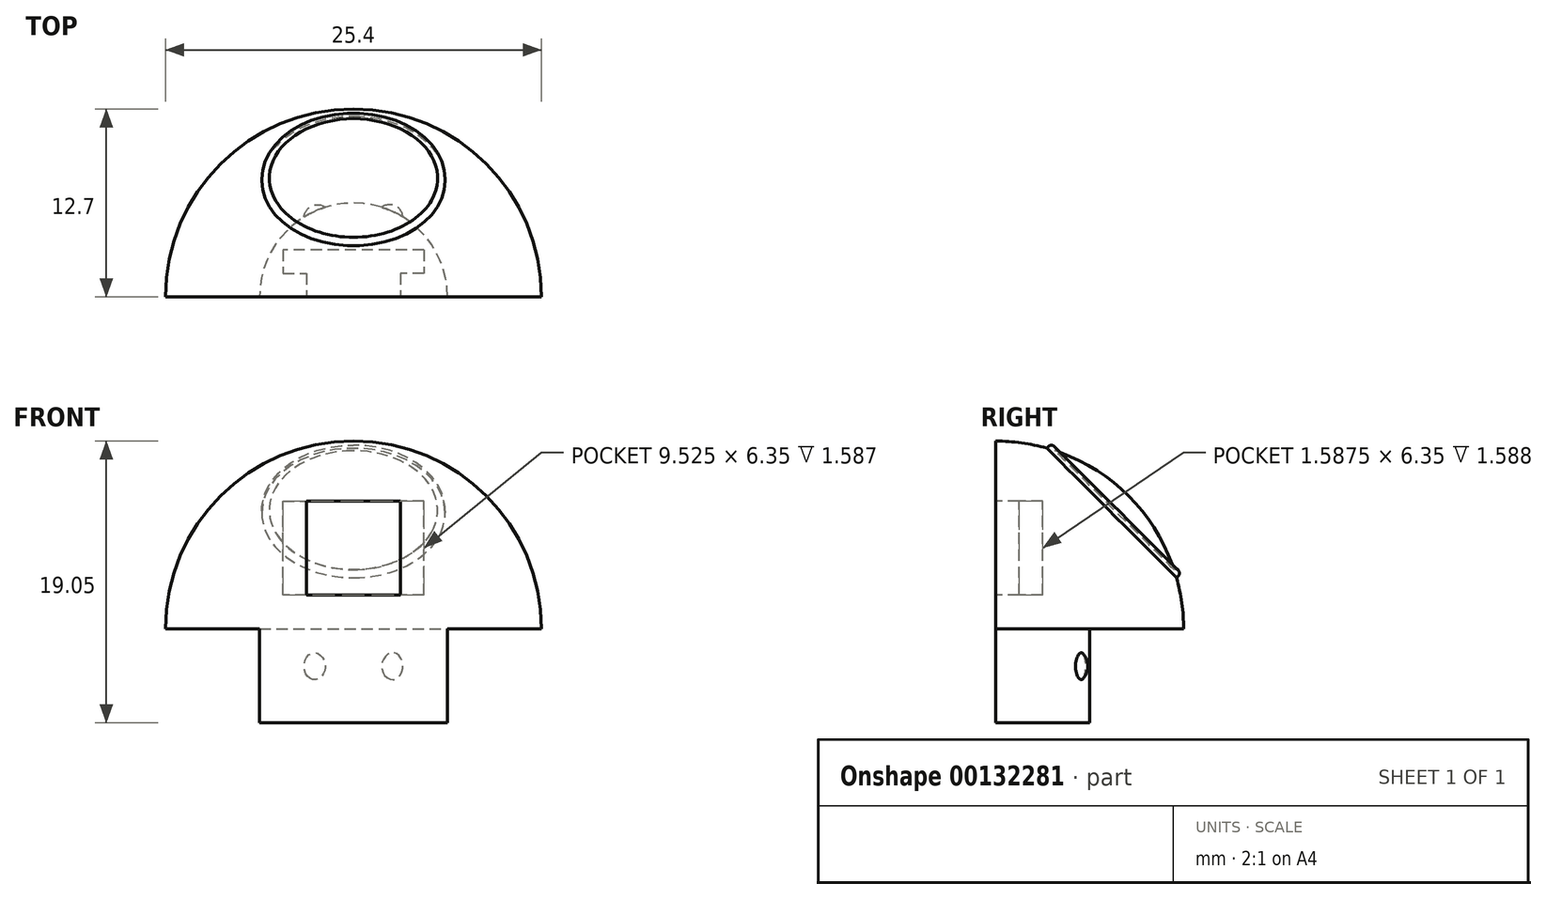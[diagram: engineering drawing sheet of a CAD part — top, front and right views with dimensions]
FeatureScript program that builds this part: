
annotation { "Feature Type Name" : "Feature", "Feature Type Description" : "" }
export const myFeature = defineFeature(function(context is Context, id is Id, definition is map)
    precondition{}
    {
        {
            var Q0;
            Q0=qCreatedBy(makeId("Front.planeOp"),FACE);
            var sketch = newSketch(context, id + "F0", { "sketchPlane" : qUnion([Q0])});
            skArc(sketch, "E0", {"start": v(12.7, 0) * mm, "mid": v(0, 12.7) * mm, "end": v(-12.7, 0) * mm});
            skLineSegment(sketch, "E1", {"start": v(-12.7, 0) * mm, "end": v(-6.35, 0) * mm});
            skLineSegment(sketch, "E2", {"start": v(6.35, 0) * mm, "end": v(12.7, 0) * mm});
            skLineSegment(sketch, "E3.0", {"start": v(-6.35, 0) * mm, "end": v(-6.35, -6.35) * mm});
            skLineSegment(sketch, "E4.0", {"start": v(6.35, 0) * mm, "end": v(6.35, -6.35) * mm});
            skLineSegment(sketch, "E5", {"start": v(6.35, -6.35) * mm, "end": v(-6.35, -6.35) * mm});
            skLineSegment(sketch, "E6", {"start": v(0, 0) * mm, "end": v(0, -6.35) * mm});
            skLineSegment(sketch, "E7", {"start": v(0, -6.35) * mm, "end": v(0, 12.7) * mm});
            skSolve(sketch);
        }
        {
            var Q0;
            {var subQ1=sQuery(id+"F0.wireOp",EDGE,"E4.0");Q0=makeQuery(id+"F0.imprint","IMPRINT",FACE,{"disambiguationData":[TD([[makeQuery(id+"F0.imprint","IMPRINT",EDGE,{"derivedFrom":subQ1}),-1.0]])]});}
            var Q1;
            Q1=sQuery(id+"F0.wireOp",EDGE,"E7");
            revolve(context, id + "F1", {"entities" : qUnion([Q0]), "axis" : qUnion([Q1]), "revolveType" : RevolveType.ONE_DIRECTION, "angle" : 180 * degree});
        }
        {
            var Q0;
            Q0=makeQuery(id+"F1.opRevolve","CAP_FACE",FACE,{"disambiguationData":[OSD([sQuery(id+"F0.wireOp",EDGE,"E0"),sQuery(id+"F0.wireOp",EDGE,"E4.0"),sQuery(id+"F0.wireOp",EDGE,"E2"),sQuery(id+"F0.wireOp",EDGE,"E5"),sQuery(id+"F0.wireOp",EDGE,"E7")])],"isStart":false});
            var sketch = newSketch(context, id + "F2", { "sketchPlane" : qUnion([Q0])});
            skSolve(sketch);
        }
        {
            var Q0;
            Q0=makeQuery(id+"F1.opRevolve","CAP_FACE",FACE,{"disambiguationData":[OSD([sQuery(id+"F0.wireOp",EDGE,"E0"),sQuery(id+"F0.wireOp",EDGE,"E4.0"),sQuery(id+"F0.wireOp",EDGE,"E2"),sQuery(id+"F0.wireOp",EDGE,"E5"),sQuery(id+"F0.wireOp",EDGE,"E7")])],"isStart":false});
            cPlane(context, id + "F3", {"entities" : qUnion([Q0]), "cplaneType" : CPlaneType.OFFSET, "offset" : 5.33 * mm, "oppositeDirection" : true, "width" : 152.4 * mm, "height" : 152.4 * mm});
        }
        {
            var Q0;
            Q0=qCreatedBy(id+"F3.planeOp",FACE);
            var sketch = newSketch(context, id + "F4", { "sketchPlane" : qUnion([Q0])});
            skArc(sketch, "E8.0", {"start": v(2.44, -3.7) * mm, "mid": v(1.54, -2.52) * mm, "end": v(2.44, -1.35) * mm});
            skLineSegment(sketch, "E8.1", {"start": v(2.44, -1.35) * mm, "end": v(2.44, -3.7) * mm});
            skPoint(sketch, "E8.2.end.orphan", {"position": v(2.44, -1.35) * mm});
            skPoint(sketch, "E8.2.start.orphan", {"position": v(2.44, -3.7) * mm});
            skSolve(sketch);
        }
        {
            var Q0;
            Q0 = qSketchRegion(id + "F4", true);
            var Q1;
            Q1=sQuery(id+"F4.wireOp",EDGE,"E8.1");
            revolve(context, id + "F5", {"operationType" : NewBodyOperationType.ADD, "entities" : qUnion([Q0]), "axis" : qUnion([Q1]), "revolveType" : RevolveType.FULL});
        }
        {
            var Q0;
            Q0=qCreatedBy(id+"F3.planeOp",FACE);
            var sketch = newSketch(context, id + "F6", { "sketchPlane" : qUnion([Q0])});
            skLineSegment(sketch, "E9.0", {"start": v(-2.44, -1.35) * mm, "end": v(-2.44, -3.7) * mm});
            skArc(sketch, "E9.1", {"start": v(-2.44, -3.7) * mm, "mid": v(-1.54, -2.52) * mm, "end": v(-2.44, -1.35) * mm});
            skSolve(sketch);
        }
        {
            var Q0;
            Q0 = qSketchRegion(id + "F6", true);
            var Q1;
            Q1=sQuery(id+"F6.wireOp",EDGE,"E9.0");
            revolve(context, id + "F7", {"operationType" : NewBodyOperationType.ADD, "entities" : qUnion([Q0]), "axis" : qUnion([Q1]), "revolveType" : RevolveType.FULL});
        }
        {
            var Q0;
            Q0=qCreatedBy(makeId("Right.planeOp"),FACE);
            var sketch = newSketch(context, id + "F8", { "sketchPlane" : qUnion([Q0])});
            skLineSegment(sketch, "E10.0", {"start": v(0, 0) * mm, "end": v(0, 12.7) * mm});
            skLineSegment(sketch, "E10.1", {"start": v(0, 0) * mm, "end": v(12.7, 0) * mm});
            skSolve(sketch);
        }
        {
            var Q0;
            Q0=makeQuery(id+"F2.imprint","IMPRINT",FACE,{"disambiguationData":[TD([[makeQuery(id+"F2.imprint","IMPRINT",EDGE,{"derivedFrom":makeQuery(id+"F1.opRevolve","CAP_EDGE",EDGE,{"disambiguationData":[OSD([sQuery(id+"F0.wireOp",EDGE,"E0")])],"isStart":false})}),-1.0]])]});
            cPlane(context, id + "F9", {"entities" : qUnion([Q0]), "cplaneType" : CPlaneType.OFFSET, "offset" : 6.35 * mm, "oppositeDirection" : true, "width" : 152.4 * mm, "height" : 152.4 * mm});
        }
        {
            var Q0;
            Q0=qCreatedBy(id+"F9.planeOp",FACE);
            var sketch = newSketch(context, id + "F10", { "sketchPlane" : qUnion([Q0])});
            skPoint(sketch, "E11.0", {"position": v(0, 0) * mm});
            skLineSegment(sketch, "E12.0", {"start": v(12.7, 0) * mm, "end": v(-12.7, 0) * mm});
            skLineSegment(sketch, "E12.1", {"start": v(0, 0) * mm, "end": v(0, 12.7) * mm});
            skLineSegment(sketch, "E13", {"start": v(0, 6.35) * mm, "end": v(13.47, 6.35) * mm});
            skPoint(sketch, "E13.endSnap0", {"position": v(0, 6.35) * mm});
            skSolve(sketch);
        }
        {
            var Q0;
            Q0=sQuery(id+"F8.wireOp",VERTEX,"E10.0.end");
            var Q1;
            Q1=sQuery(id+"F8.wireOp",VERTEX,"E10.1.end");
            var Q2;
            Q2=sQuery(id+"F10.wireOp",VERTEX,"E13.end");
            cPlane(context, id + "F11", {"entities" : qUnion([Q0, Q1, Q2]), "cplaneType" : CPlaneType.THREE_POINT, "offset" : 0 * mm, "width" : 152.4 * mm, "height" : 152.4 * mm});
        }
        {
            var Q0;
            Q0=qCreatedBy(id+"F11.planeOp",FACE);
            var sketch = newSketch(context, id + "F12", { "sketchPlane" : qUnion([Q0])});
            skCircle(sketch, "E14", {"center": v(0, 0) * mm, "radius": 5.69 * mm});
            skCircle(sketch, "E15.0", {"center": v(0, 0) * mm, "radius": 6.2 * mm});
            skSolve(sketch);
        }
        {
            var Q0;
            Q0 = qSketchRegion(id + "F12", true);
            extrude(context, id + "F13", {"entities" : qUnion([Q0]), "operationType" : NewBodyOperationType.ADD, "depth" : 2.54 * mm});
        }
        {
            var Q0;
            Q0=makeQuery(id+"F13.opExtrude","CAP_EDGE",EDGE,{"disambiguationData":[OSD([sQuery(id+"F12.wireOp",EDGE,"E15.0")])],"isStart":false});
            var Q1;
            Q1=makeQuery(id+"F13.opExtrude","CAP_EDGE",EDGE,{"disambiguationData":[OSD([sQuery(id+"F12.wireOp",EDGE,"E14")])],"isStart":false});
            fillet(context, id + "F14", {"entities" : qUnion([Q0, Q1]), "radius" : 0.25 * mm, "tangentPropagation" : true, "allowEdgeOverflow" : false});
        }
        {
            var Q0;
            Q0=qCreatedBy(makeId("Right.planeOp"),FACE);
            cPlane(context, id + "F15", {"entities" : qUnion([Q0]), "cplaneType" : CPlaneType.OFFSET, "offset" : 5.08 * mm, "width" : 152.4 * mm, "height" : 152.4 * mm});
        }
        {
            var Q0;
            Q0=qCreatedBy(id+"F15.planeOp",FACE);
            var sketch = newSketch(context, id + "F16", { "sketchPlane" : qUnion([Q0])});
            skArc(sketch, "E16", {"start": v(0, 1.12) * mm, "mid": v(5.2, 6.33) * mm, "end": v(0, 11.54) * mm});
            skArc(sketch, "E17", {"start": v(0, 0.68) * mm, "mid": v(5.66, 6.33) * mm, "end": v(0, 11.99) * mm});
            skLineSegment(sketch, "E18", {"start": v(0, 11.54) * mm, "end": v(0, 1.12) * mm});
            skLineSegment(sketch, "E19", {"start": v(0, 11.99) * mm, "end": v(0, 0.68) * mm});
            skSolve(sketch);
        }
        {
            var Q0;
            Q0=qCreatedBy(makeId("Right.planeOp"),FACE);
            cPlane(context, id + "F17", {"entities" : qUnion([Q0]), "cplaneType" : CPlaneType.OFFSET, "offset" : 5.08 * mm, "oppositeDirection" : true, "width" : 152.4 * mm, "height" : 152.4 * mm});
        }
        {
            var Q0;
            Q0=makeQuery(id+"F1.opRevolve","CAP_FACE",FACE,{"disambiguationData":[OSD([sQuery(id+"F0.wireOp",EDGE,"E0"),sQuery(id+"F0.wireOp",EDGE,"E4.0"),sQuery(id+"F0.wireOp",EDGE,"E2"),sQuery(id+"F0.wireOp",EDGE,"E5"),sQuery(id+"F0.wireOp",EDGE,"E7")])],"isStart":false});
            var sketch = newSketch(context, id + "F18", { "sketchPlane" : qUnion([Q0])});
            skLineSegment(sketch, "E20.bottom", {"start": v(3.18, 2.3) * mm, "end": v(-3.18, 2.3) * mm});
            skLineSegment(sketch, "E20.top", {"start": v(3.18, 8.65) * mm, "end": v(-3.17, 8.65) * mm});
            skLineSegment(sketch, "E20.left", {"start": v(3.18, 2.3) * mm, "end": v(3.18, 8.65) * mm});
            skLineSegment(sketch, "E20.right", {"start": v(-3.17, 2.3) * mm, "end": v(-3.17, 8.65) * mm});
            skPoint(sketch, "E20.middle", {"position": v(0, 5.48) * mm});
            skSolve(sketch);
        }
        {
            var Q0;
            Q0 = qSketchRegion(id + "F18", true);
            extrude(context, id + "F19", {"entities" : qUnion([Q0]), "operationType" : NewBodyOperationType.REMOVE, "oppositeDirection" : true, "depth" : 3.17 * mm});
        }
        {
            var Q0;
            Q0=makeQuery(id+"F19.boolean.opBoolean","COPY",FACE,{"derivedFrom":makeQuery(id+"F19.opExtrude","SWEPT_FACE",FACE,{"disambiguationData":[OSD([sQuery(id+"F18.wireOp",EDGE,"E20.left")])]})});
            var sketch = newSketch(context, id + "F20", { "sketchPlane" : qUnion([Q0])});
            skLineSegment(sketch, "E21.bottom", {"start": v(-3.18, 2.3) * mm, "end": v(-1.59, 2.3) * mm});
            skLineSegment(sketch, "E21.top", {"start": v(-3.18, 8.65) * mm, "end": v(-1.59, 8.65) * mm});
            skLineSegment(sketch, "E21.left", {"start": v(-3.18, 2.3) * mm, "end": v(-3.18, 8.65) * mm});
            skLineSegment(sketch, "E21.right", {"start": v(-1.59, 2.3) * mm, "end": v(-1.59, 8.65) * mm});
            skSolve(sketch);
        }
        {
            var Q0;
            Q0=makeQuery(id+"F19.boolean.opBoolean","COPY",FACE,{"derivedFrom":makeQuery(id+"F19.opExtrude","SWEPT_FACE",FACE,{"disambiguationData":[OSD([sQuery(id+"F18.wireOp",EDGE,"E20.right")])]})});
            var sketch = newSketch(context, id + "F21", { "sketchPlane" : qUnion([Q0])});
            skLineSegment(sketch, "E22.bottom", {"start": v(3.18, 2.3) * mm, "end": v(1.59, 2.3) * mm});
            skLineSegment(sketch, "E22.top", {"start": v(3.18, 8.65) * mm, "end": v(1.59, 8.65) * mm});
            skLineSegment(sketch, "E22.left", {"start": v(3.18, 2.3) * mm, "end": v(3.18, 8.65) * mm});
            skLineSegment(sketch, "E22.right", {"start": v(1.59, 2.3) * mm, "end": v(1.59, 8.65) * mm});
            skSolve(sketch);
        }
        {
            var Q0;
            Q0 = qSketchRegion(id + "F21", true);
            extrude(context, id + "F22", {"entities" : qUnion([Q0]), "operationType" : NewBodyOperationType.REMOVE, "oppositeDirection" : true, "depth" : 1.59 * mm});
        }
        {
            var Q0;
            Q0 = qSketchRegion(id + "F20", true);
            extrude(context, id + "F23", {"entities" : qUnion([Q0]), "operationType" : NewBodyOperationType.REMOVE, "oppositeDirection" : true, "depth" : 1.59 * mm});
        }
    });
